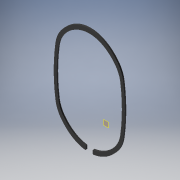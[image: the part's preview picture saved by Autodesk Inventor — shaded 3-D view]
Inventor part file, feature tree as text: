
AUTODESK INVENTOR PART (.ipt)
format: ipt  version: 2018 (Build 220112000, 112)  size: 194,048 bytes
history: native  units: in
note: dims shown in document units (in); Inventor stores cm internally (conversion verified against a paired STEP export)
features: other x4, extrude x3, sketch x3, reference x3, plane x1, fillet x1
ambient origin geometry x8: Origin, YZ Plane, XZ Plane, XY Plane, X Axis, Y Axis, Z Axis, Center Point
bodies: Solid1 (feature_tree)
feature tree (15):
  plane  "Work Plane2"
  extrude  "Extrusion1"  Depth=0.25in TaperAngle=0.0deg
  extrude  "Extrusion2"  Depth=0.0787in
  extrude  "Extrusion3"  [1 undecoded]
  fillet  "Fillet1"  [1 undecoded]
  sketch  "Sketch1"  dims[d0=0.25in d1=0.0in d2=0.25in d3=0.0in]
  sketch  "Sketch2"  dims[d4=0.25in d5=0.0in d6=0.0787in]
  sketch  "Sketch3"
  reference  "Reference2"
  reference  "Reference3"
  reference  "Reference4"
  other  "<userpath>\OneDrive\Documents\Inventor\TSA\2018\Animatronics\Tortoise\Turtle3.iam"
  other  "Turtle3.iam"
  other  "Frame - Copy:1"
  other  "Tail_Mount:1"
note: 2 required parameter values undecoded (feature->parameter linkage not recoverable at this tier; creation-order binding heuristic only, values carry confidence <= 0.55)
